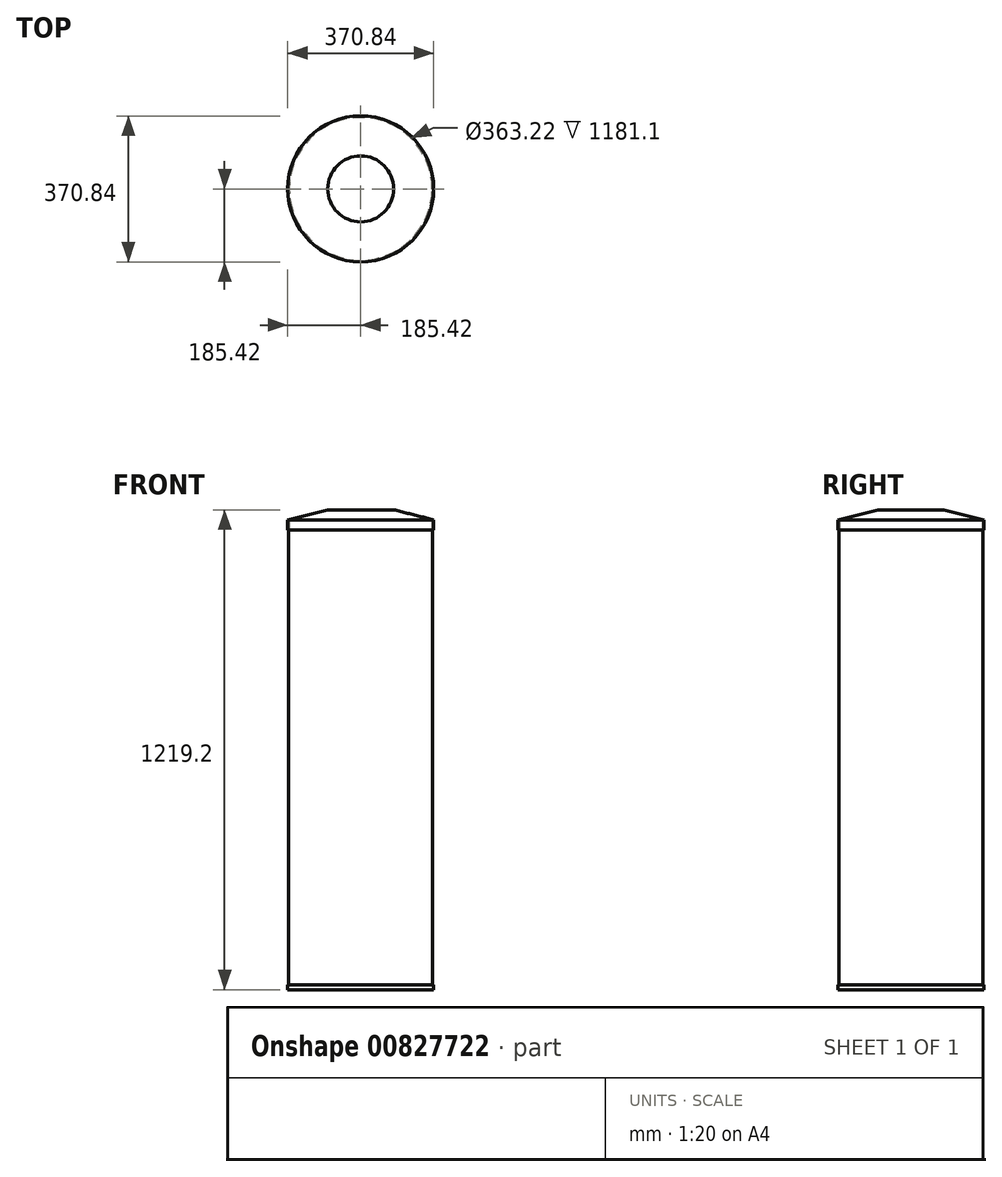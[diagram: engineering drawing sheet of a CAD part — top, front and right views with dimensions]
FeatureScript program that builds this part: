
annotation { "Feature Type Name" : "Feature", "Feature Type Description" : "" }
export const myFeature = defineFeature(function(context is Context, id is Id, definition is map)
    precondition{}
    {
        {
            var Q0;
            Q0=qCreatedBy(makeId("Top.planeOp"),FACE);
            var sketch = newSketch(context, id + "F0", { "sketchPlane" : qUnion([Q0])});
            skCircle(sketch, "E0", {"center": v(0, 0) * mm, "radius": 185.42 * mm});
            skSolve(sketch);
        }
        {
            var Q0;
            Q0=makeQuery(id+"F0.imprint","IMPRINT",FACE,{"disambiguationData":[TD([[makeQuery(id+"F0.imprint","IMPRINT",EDGE,{"derivedFrom":sQuery(id+"F0.wireOp",EDGE,"E0")}),1.0]])]});
            extrude(context, id + "F1", {"entities" : qUnion([Q0]), "depth" : 12.7 * mm, "offsetDistance" : 25.4 * mm});
        }
        {
            var Q0;
            Q0=makeQuery(id+"F1.opExtrude","CAP_FACE",FACE,{"disambiguationData":[OSD([sQuery(id+"F0.wireOp",EDGE,"E0")])],"isStart":false});
            var sketch = newSketch(context, id + "F2", { "sketchPlane" : qUnion([Q0])});
            skCircle(sketch, "E1", {"center": v(0, 0) * mm, "radius": 182.88 * mm});
            skCircle(sketch, "E2", {"center": v(0, 0) * mm, "radius": 181.61 * mm});
            skSolve(sketch);
        }
        {
            var Q0;
            Q0=qSketchRegion(id+"F2",true);
            extrude(context, id + "F3", {"entities" : qUnion([Q0]), "operationType" : NewBodyOperationType.ADD, "depth" : 1181.1 * mm, "offsetDistance" : 25.4 * mm});
        }
        {
            var Q0;
            Q0=makeQuery(id+"F3.opExtrude","CAP_FACE",FACE,{"disambiguationData":[OSD([sQuery(id+"F2.wireOp",EDGE,"E1"),sQuery(id+"F2.wireOp",EDGE,"E2")])],"isStart":false});
            var sketch = newSketch(context, id + "F4", { "sketchPlane" : qUnion([Q0])});
            skCircle(sketch, "E3", {"center": v(0, 0) * mm, "radius": 185.42 * mm});
            skSolve(sketch);
        }
        {
            var Q0;
            Q0=qSketchRegion(id+"F4",true);
            extrude(context, id + "F5", {"entities" : qUnion([Q0]), "operationType" : NewBodyOperationType.ADD, "depth" : 25.4 * mm, "offsetDistance" : 25.4 * mm});
        }
        {
            var Q0;
            Q0=makeQuery(id+"F5.opExtrude","CAP_EDGE",EDGE,{"disambiguationData":[OSD([sQuery(id+"F4.wireOp",EDGE,"E3")])],"isStart":false});
            chamfer(context, id + "F6", {"entities" : qUnion([Q0]), "chamferType" : ChamferType.TWO_OFFSETS, "width1" : 101.6 * mm, "oppositeDirection" : false, "width2" : 25.4 * mm});
        }
        {
            var Q0;
            {var subQ0=sQuery(id+"F4.wireOp",EDGE,"E3");Q0=makeQuery(id+"F5.boolean.opBoolean","SPLIT",FACE,{"disambiguationData":[TD([makeQuery(id+"F3.opExtrude","SWEPT_FACE",FACE,{"disambiguationData":[OSD([sQuery(id+"F2.wireOp",EDGE,"E1")])]})])],"derivedFrom":makeQuery(id+"F5.opExtrude","CAP_FACE",FACE,{"disambiguationData":[OSD([subQ0])],"isStart":true})});}
            var sketch = newSketch(context, id + "F7", { "sketchPlane" : qUnion([Q0])});
            skCircle(sketch, "E4.0", {"center": v(0, 0) * mm, "radius": 182.88 * mm});
            skCircle(sketch, "E5.0.0", {"center": v(0, 0) * mm, "radius": 185.42 * mm});
            skSolve(sketch);
        }
        {
            var Q0;
            Q0=qSketchRegion(id+"F7",true);
            extrude(context, id + "F8", {"entities" : qUnion([Q0]), "operationType" : NewBodyOperationType.ADD, "depth" : 25.4 * mm, "offsetDistance" : 25.4 * mm});
        }
    });
